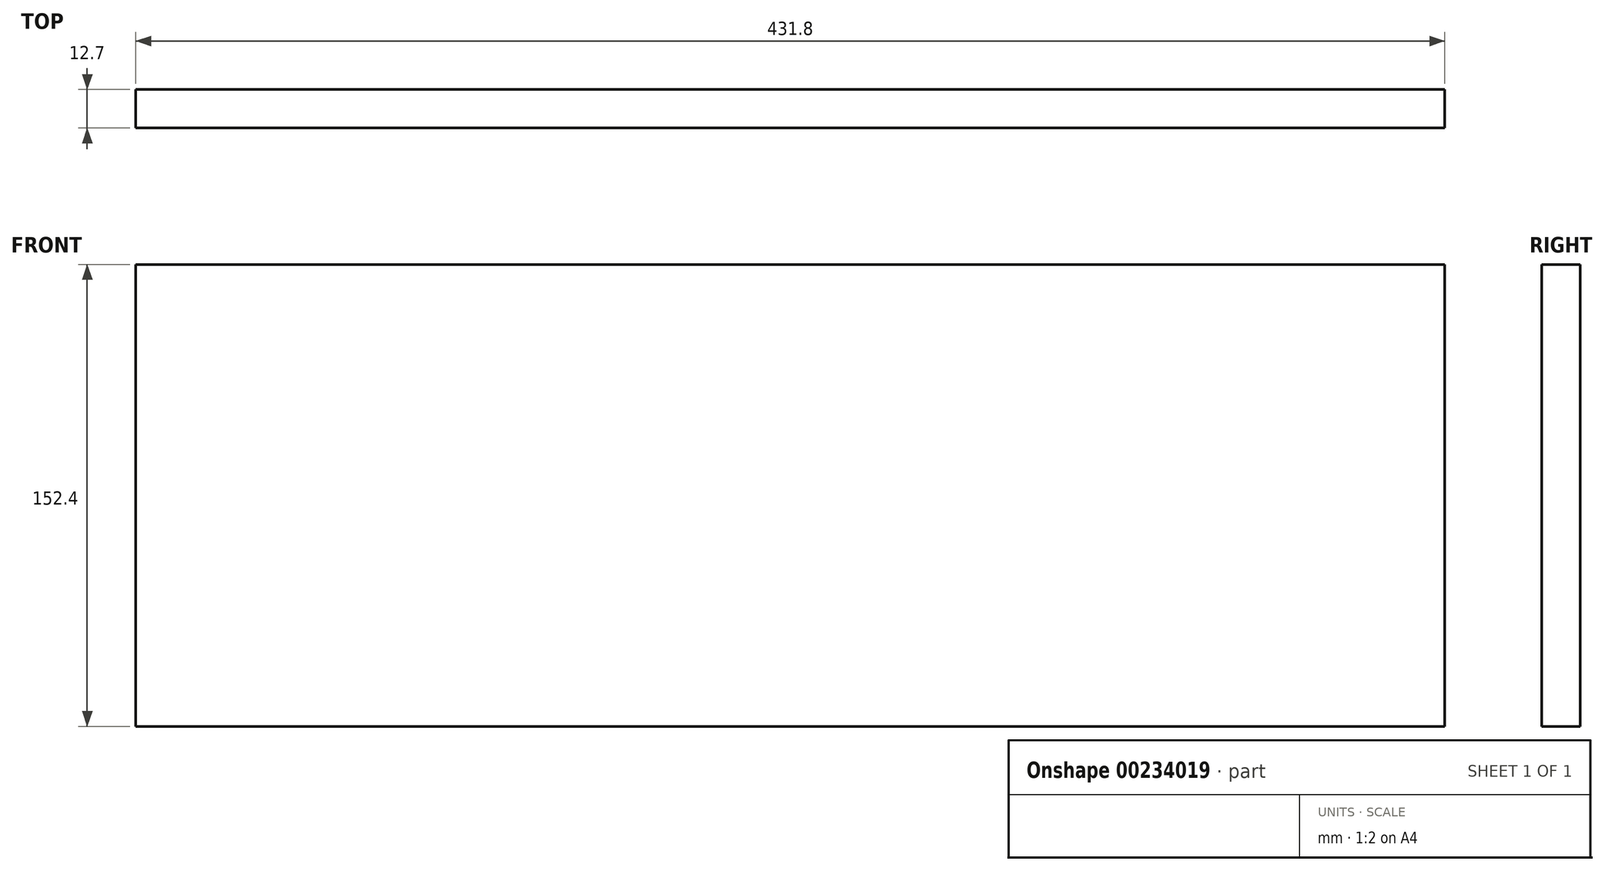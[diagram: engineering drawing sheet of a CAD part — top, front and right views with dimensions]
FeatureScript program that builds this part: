
annotation { "Feature Type Name" : "Feature", "Feature Type Description" : "" }
export const myFeature = defineFeature(function(context is Context, id is Id, definition is map)
    precondition{}
    {
        {
            var Q0;
            Q0=qCreatedBy(makeId("Front.planeOp"),FACE);
            var sketch = newSketch(context, id + "F0", { "sketchPlane" : qUnion([Q0])});
            skLineSegment(sketch, "E0.bottom", {"start": v(-206, 87.48) * mm, "end": v(225.8, 87.48) * mm});
            skLineSegment(sketch, "E0.top", {"start": v(-206, -64.92) * mm, "end": v(225.8, -64.92) * mm});
            skLineSegment(sketch, "E0.left", {"start": v(-206, 87.48) * mm, "end": v(-206, -64.92) * mm});
            skLineSegment(sketch, "E0.right", {"start": v(225.8, 87.48) * mm, "end": v(225.8, -64.92) * mm});
            skSolve(sketch);
        }
        {
            var Q0;
            Q0 = qSketchRegion(id + "F0", true);
            extrude(context, id + "F1", {"entities" : qUnion([Q0]), "depth" : 12.7 * mm});
        }
    });
